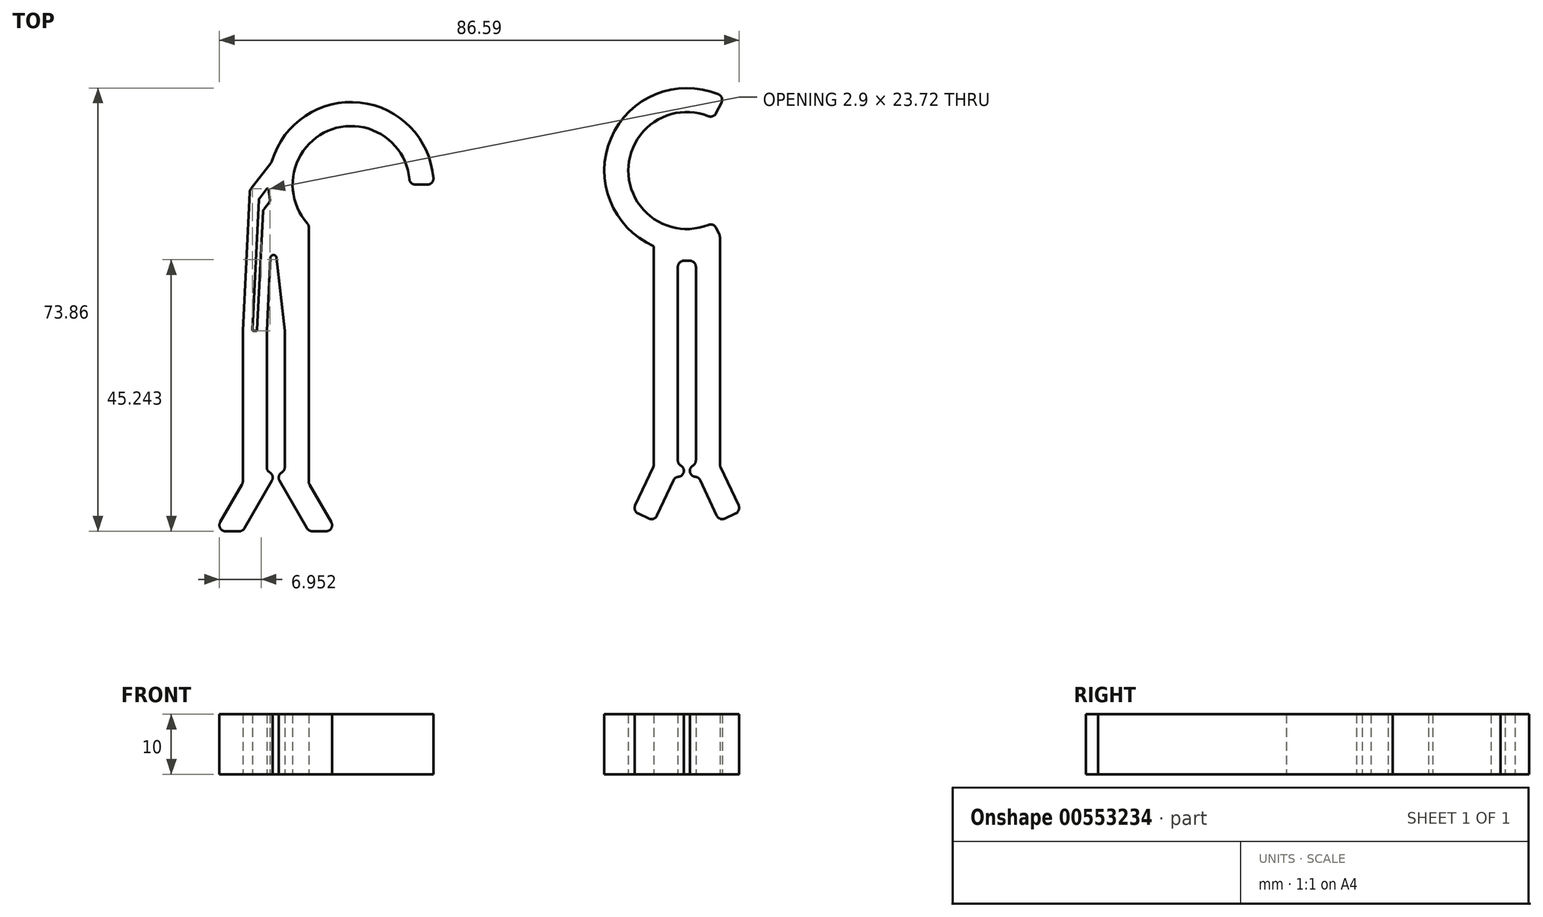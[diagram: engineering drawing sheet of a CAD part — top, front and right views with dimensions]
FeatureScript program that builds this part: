
annotation { "Feature Type Name" : "Feature", "Feature Type Description" : "" }
export const myFeature = defineFeature(function(context is Context, id is Id, definition is map)
    precondition{}
    {
        {
            var Q0;
            Q0=qCreatedBy(makeId("Top.planeOp"),FACE);
            var sketch = newSketch(context, id + "F0", { "sketchPlane" : qUnion([Q0])});
            skArc(sketch, "E0", {"start": v(-22.14, 7.9) * mm, "mid": v(-35.71, 15.97) * mm, "end": v(-39.15, 0.56) * mm});
            skArc(sketch, "E1", {"start": v(-18.14, 8.07) * mm, "mid": v(-30.38, 20.69) * mm, "end": v(-45.02, 10.95) * mm});
            skLineSegment(sketch, "E2", {"start": v(-42.9, -17.37) * mm, "end": v(-42.9, -40.1) * mm});
            skLineSegment(sketch, "E3", {"start": v(-38.9, -4.79) * mm, "end": v(-38.9, -0.1) * mm});
            skLineSegment(sketch, "E4", {"start": v(-21.16, 7.02) * mm, "end": v(-19.12, 7.02) * mm});
            skLineSegment(sketch, "E5", {"start": v(-49.9, -41.7) * mm, "end": v(-49.9, -17.37) * mm});
            skLineSegment(sketch, "E6", {"start": v(-42.9, -17.37) * mm, "end": v(-44.3, -5.15) * mm});
            skPoint(sketch, "E7.visualSharp", {"position": v(-18.1, 7.02) * mm});
            skArc(sketch, "E7.filletArc", {"start": v(-19.12, 7.02) * mm, "mid": v(-18.4, 7.33) * mm, "end": v(-18.14, 8.07) * mm});
            skPoint(sketch, "E8.visualSharp", {"position": v(-22.1, 7.02) * mm});
            skArc(sketch, "E8.filletArc", {"start": v(-22.14, 7.9) * mm, "mid": v(-21.82, 7.27) * mm, "end": v(-21.16, 7.02) * mm});
            skPoint(sketch, "E9.visualSharp", {"position": v(-38.9, 0.29) * mm});
            skArc(sketch, "E9.filletArc", {"start": v(-38.9, -0.1) * mm, "mid": v(-38.97, 0.25) * mm, "end": v(-39.15, 0.56) * mm});
            skArc(sketch, "E10", {"start": v(-45.04, -42.33) * mm, "mid": v(-44.94, -41.57) * mm, "end": v(-45.4, -40.96) * mm});
            skArc(sketch, "E11", {"start": v(-43.4, -40.96) * mm, "mid": v(-43.87, -41.57) * mm, "end": v(-43.77, -42.33) * mm});
            skLineSegment(sketch, "E12.trimOffspring", {"start": v(-45.9, -40.1) * mm, "end": v(-45.9, -17.37) * mm});
            skPoint(sketch, "E13.visualSharp", {"position": v(-42.9, -40.83) * mm});
            skArc(sketch, "E13.filletArc", {"start": v(-43.4, -40.96) * mm, "mid": v(-43.04, -40.6) * mm, "end": v(-42.9, -40.1) * mm});
            skPoint(sketch, "E14.visualSharp", {"position": v(-45.9, -40.83) * mm});
            skArc(sketch, "E14.filletArc", {"start": v(-45.9, -40.1) * mm, "mid": v(-45.77, -40.6) * mm, "end": v(-45.4, -40.96) * mm});
            skLineSegment(sketch, "E15", {"start": v(-45.9, -17.37) * mm, "end": v(-45.3, -5.18) * mm});
            skLineSegment(sketch, "E16", {"start": v(-47.5, -17.18) * mm, "end": v(-46.7, -1.36) * mm});
            skLineSegment(sketch, "E17", {"start": v(-49.9, -17.37) * mm, "end": v(-48.97, 1.3) * mm});
            skLineSegment(sketch, "E18", {"start": v(-48.28, -17) * mm, "end": v(-47.47, -0.76) * mm});
            skLineSegment(sketch, "E19", {"start": v(-48.28, -17) * mm, "end": v(-48.3, -17.16) * mm});
            skLineSegment(sketch, "E20", {"start": v(-48.1, -17.37) * mm, "end": v(-47.7, -17.37) * mm});
            skLineSegment(sketch, "E21", {"start": v(-46.7, -1.36) * mm, "end": v(-46.5, 2.6) * mm});
            skLineSegment(sketch, "E22", {"start": v(-46.4, 2.88) * mm, "end": v(-45.5, 4.05) * mm});
            skLineSegment(sketch, "E23", {"start": v(-47.47, -0.76) * mm, "end": v(-47.2, 4.48) * mm});
            skLineSegment(sketch, "E24", {"start": v(-47.1, 4.76) * mm, "end": v(-45.93, 6.28) * mm});
            skLineSegment(sketch, "E25", {"start": v(-48.97, 1.3) * mm, "end": v(-48.75, 5.75) * mm});
            skLineSegment(sketch, "E26", {"start": v(-48.54, 6.31) * mm, "end": v(-45.2, 10.62) * mm});
            skArc(sketch, "E27.trimOffspring", {"start": v(-45.57, 6.17) * mm, "mid": v(-45.54, 5.81) * mm, "end": v(-45.5, 5.46) * mm});
            skLineSegment(sketch, "E28.trimOffspring", {"start": v(-45.39, 4.41) * mm, "end": v(-45.5, 5.46) * mm});
            skPoint(sketch, "E29.visualSharp", {"position": v(-45.07, 10.77) * mm});
            skArc(sketch, "E29.filletArc", {"start": v(-45.2, 10.62) * mm, "mid": v(-45.1, 10.78) * mm, "end": v(-45.02, 10.95) * mm});
            skPoint(sketch, "E30.visualSharp", {"position": v(-48.73, 6.07) * mm});
            skArc(sketch, "E30.filletArc", {"start": v(-48.54, 6.31) * mm, "mid": v(-48.69, 6.05) * mm, "end": v(-48.75, 5.75) * mm});
            skPoint(sketch, "E31.visualSharp", {"position": v(-49.9, -42.83) * mm});
            skPoint(sketch, "E32.visualSharp", {"position": v(-44.99, 0.9) * mm});
            skArc(sketch, "E32.filletArc", {"start": v(-44.3, -5.15) * mm, "mid": v(-44.8, -4.7) * mm, "end": v(-45.3, -5.18) * mm});
            skPoint(sketch, "E33.visualSharp", {"position": v(-47.2, 4.64) * mm});
            skArc(sketch, "E33.filletArc", {"start": v(-47.1, 4.76) * mm, "mid": v(-47.18, 4.63) * mm, "end": v(-47.2, 4.48) * mm});
            skPoint(sketch, "E34.visualSharp", {"position": v(-45.37, 4.21) * mm});
            skArc(sketch, "E34.filletArc", {"start": v(-45.5, 4.05) * mm, "mid": v(-45.4, 4.22) * mm, "end": v(-45.39, 4.41) * mm});
            skPoint(sketch, "E35.visualSharp", {"position": v(-46.5, 2.75) * mm});
            skArc(sketch, "E35.filletArc", {"start": v(-46.4, 2.88) * mm, "mid": v(-46.48, 2.75) * mm, "end": v(-46.5, 2.6) * mm});
            skPoint(sketch, "E36.visualSharp", {"position": v(-48.3, -17.37) * mm});
            skArc(sketch, "E36.filletArc", {"start": v(-48.3, -17.16) * mm, "mid": v(-48.24, -17.3) * mm, "end": v(-48.1, -17.37) * mm});
            skPoint(sketch, "E37.visualSharp", {"position": v(-47.5, -17.37) * mm});
            skArc(sketch, "E37.filletArc", {"start": v(-47.7, -17.37) * mm, "mid": v(-47.56, -17.31) * mm, "end": v(-47.5, -17.18) * mm});
            skPoint(sketch, "E38.visualSharp", {"position": v(-45.6, 6.7) * mm});
            skArc(sketch, "E38.filletArc", {"start": v(-45.57, 6.17) * mm, "mid": v(-45.71, 6.35) * mm, "end": v(-45.93, 6.28) * mm});
            skLineSegment(sketch, "E39", {"start": v(-49.9, -41.7) * mm, "end": v(-49.9, -42.49) * mm});
            skLineSegment(sketch, "E40", {"start": v(-49.61, -50.25) * mm, "end": v(-45.04, -42.33) * mm});
            skLineSegment(sketch, "E41", {"start": v(-43.77, -42.33) * mm, "end": v(-39.2, -50.25) * mm});
            skPoint(sketch, "E42.start.orphan", {"position": v(-45.9, -42.83) * mm});
            skPoint(sketch, "E43.orphan", {"position": v(-42.9, -42.83) * mm});
            skLineSegment(sketch, "E44", {"start": v(-53.66, -49.25) * mm, "end": v(-50.04, -42.99) * mm});
            skLineSegment(sketch, "E45", {"start": v(-50.48, -50.75) * mm, "end": v(-52.79, -50.75) * mm});
            skPoint(sketch, "E46.visualSharp", {"position": v(-49.9, -50.75) * mm});
            skArc(sketch, "E46.filletArc", {"start": v(-50.48, -50.75) * mm, "mid": v(-49.98, -50.62) * mm, "end": v(-49.61, -50.25) * mm});
            skPoint(sketch, "E47.visualSharp", {"position": v(-54.52, -50.75) * mm});
            skArc(sketch, "E47.filletArc", {"start": v(-53.66, -49.25) * mm, "mid": v(-53.66, -50.25) * mm, "end": v(-52.79, -50.75) * mm});
            skPoint(sketch, "E48.visualSharp", {"position": v(-49.9, -42.75) * mm});
            skArc(sketch, "E48.filletArc", {"start": v(-50.04, -42.99) * mm, "mid": v(-49.94, -42.75) * mm, "end": v(-49.9, -42.49) * mm});
            skLineSegment(sketch, "E49", {"start": v(-35.15, -49.25) * mm, "end": v(-38.77, -42.99) * mm});
            skLineSegment(sketch, "E50", {"start": v(-38.33, -50.75) * mm, "end": v(-36.02, -50.75) * mm});
            skPoint(sketch, "E51.visualSharp", {"position": v(-38.9, -50.75) * mm});
            skArc(sketch, "E51.filletArc", {"start": v(-39.2, -50.25) * mm, "mid": v(-38.83, -50.62) * mm, "end": v(-38.33, -50.75) * mm});
            skLineSegment(sketch, "E52", {"start": v(-38.9, -4.79) * mm, "end": v(-38.9, -42.49) * mm});
            skPoint(sketch, "E53.visualSharp", {"position": v(-34.28, -50.75) * mm});
            skArc(sketch, "E53.filletArc", {"start": v(-36.02, -50.75) * mm, "mid": v(-35.15, -50.25) * mm, "end": v(-35.15, -49.25) * mm});
            skPoint(sketch, "E54.visualSharp", {"position": v(-38.9, -42.75) * mm});
            skArc(sketch, "E54.filletArc", {"start": v(-38.9, -42.49) * mm, "mid": v(-38.87, -42.75) * mm, "end": v(-38.77, -42.99) * mm});
            skLineSegment(sketch, "E55", {"start": v(24.1, -5.69) * mm, "end": v(23.6, -5.69) * mm});
            skLineSegment(sketch, "E56", {"start": v(22.6, -6.69) * mm, "end": v(22.6, -38.96) * mm});
            skLineSegment(sketch, "E57", {"start": v(21.87, -42.26) * mm, "end": v(19.11, -48.16) * mm});
            skLineSegment(sketch, "E58", {"start": v(17.78, -48.65) * mm, "end": v(15.97, -47.8) * mm});
            skLineSegment(sketch, "E59", {"start": v(15.49, -46.47) * mm, "end": v(18.5, -40) * mm});
            skLineSegment(sketch, "E60", {"start": v(18.6, -39.58) * mm, "end": v(18.6, -5.69) * mm});
            skLineSegment(sketch, "E61", {"start": v(24.1, -5.69) * mm, "end": v(24.1, -50.13) * mm, "construction": true});
            skPoint(sketch, "E62.end.orphan", {"position": v(25.6, -5.69) * mm});
            skPoint(sketch, "E62.start.orphan", {"position": v(25.24, -40.69) * mm});
            skArc(sketch, "E63", {"start": v(22.68, -41.69) * mm, "mid": v(23.57, -40.9) * mm, "end": v(23.1, -39.82) * mm});
            skPoint(sketch, "E64.visualSharp", {"position": v(18.7, -49.07) * mm});
            skArc(sketch, "E64.filletArc", {"start": v(17.78, -48.65) * mm, "mid": v(18.55, -48.68) * mm, "end": v(19.11, -48.16) * mm});
            skPoint(sketch, "E65.visualSharp", {"position": v(15.06, -47.38) * mm});
            skArc(sketch, "E65.filletArc", {"start": v(15.49, -46.47) * mm, "mid": v(15.45, -47.24) * mm, "end": v(15.97, -47.8) * mm});
            skPoint(sketch, "E66.visualSharp", {"position": v(18.6, -39.8) * mm});
            skArc(sketch, "E66.filletArc", {"start": v(18.5, -40) * mm, "mid": v(18.57, -39.8) * mm, "end": v(18.6, -39.58) * mm});
            skPoint(sketch, "E67.visualSharp", {"position": v(22.6, -39.69) * mm});
            skArc(sketch, "E67.filletArc", {"start": v(22.6, -38.96) * mm, "mid": v(22.73, -39.46) * mm, "end": v(23.1, -39.82) * mm});
            skPoint(sketch, "E68.visualSharp", {"position": v(22.17, -41.6) * mm});
            skArc(sketch, "E68.filletArc", {"start": v(22.68, -41.69) * mm, "mid": v(22.2, -41.86) * mm, "end": v(21.87, -42.26) * mm});
            skPoint(sketch, "E69.visualSharp", {"position": v(22.6, -5.69) * mm});
            skArc(sketch, "E69.filletArc", {"start": v(23.6, -5.69) * mm, "mid": v(22.9, -5.98) * mm, "end": v(22.6, -6.69) * mm});
            skLineSegment(sketch, "E70.MirrorCS", {"start": v(24.1, -5.69) * mm, "end": v(24.6, -5.69) * mm});
            skArc(sketch, "E71.MirrorCS", {"start": v(25.6, -38.96) * mm, "mid": v(25.46, -39.46) * mm, "end": v(25.1, -39.82) * mm});
            skArc(sketch, "E72.MirrorCS", {"start": v(29.7, -40) * mm, "mid": v(29.62, -39.8) * mm, "end": v(29.6, -39.58) * mm});
            skLineSegment(sketch, "E73.MirrorCS", {"start": v(30.41, -48.65) * mm, "end": v(32.22, -47.8) * mm});
            skArc(sketch, "E74.MirrorCS", {"start": v(25.5, -41.69) * mm, "mid": v(24.62, -40.9) * mm, "end": v(25.1, -39.82) * mm});
            skArc(sketch, "E75.MirrorCS", {"start": v(32.7, -46.47) * mm, "mid": v(32.74, -47.24) * mm, "end": v(32.22, -47.8) * mm});
            skArc(sketch, "E76.MirrorCS", {"start": v(30.41, -48.65) * mm, "mid": v(29.65, -48.68) * mm, "end": v(29.08, -48.16) * mm});
            skArc(sketch, "E77.MirrorCS", {"start": v(24.6, -5.69) * mm, "mid": v(25.3, -5.98) * mm, "end": v(25.6, -6.69) * mm});
            skArc(sketch, "E78.MirrorCS", {"start": v(25.5, -41.69) * mm, "mid": v(26, -41.86) * mm, "end": v(26.33, -42.26) * mm});
            skLineSegment(sketch, "E79.MirrorCS", {"start": v(29.6, -39.58) * mm, "end": v(29.6, -5.69) * mm});
            skPoint(sketch, "E80.MirrorP", {"position": v(33.13, -47.38) * mm});
            skPoint(sketch, "E81.MirrorP", {"position": v(29.5, -49.07) * mm});
            skPoint(sketch, "E82.MirrorP", {"position": v(26.02, -41.6) * mm});
            skPoint(sketch, "E83.MirrorP", {"position": v(29.6, -39.8) * mm});
            skPoint(sketch, "E84.MirrorP", {"position": v(25.6, -39.69) * mm});
            skLineSegment(sketch, "E85.MirrorCS", {"start": v(32.7, -46.47) * mm, "end": v(29.7, -40) * mm});
            skLineSegment(sketch, "E86.MirrorCS", {"start": v(26.33, -42.26) * mm, "end": v(29.08, -48.16) * mm});
            skLineSegment(sketch, "E87.MirrorCS", {"start": v(25.6, -6.69) * mm, "end": v(25.6, -38.96) * mm});
            skArc(sketch, "E88", {"start": v(27.7, 18.42) * mm, "mid": v(14.35, 9.36) * mm, "end": v(27.7, 0.3) * mm});
            skLineSegment(sketch, "E89", {"start": v(18.6, -5.69) * mm, "end": v(18.6, -3.25) * mm});
            skLineSegment(sketch, "E90", {"start": v(29.6, -5.69) * mm, "end": v(29.6, -1.68) * mm});
            skLineSegment(sketch, "E91", {"start": v(28.96, -0.18) * mm, "end": v(29.49, -1.22) * mm});
            skLineSegment(sketch, "E92", {"start": v(24.1, 9.36) * mm, "end": v(44.8, 9.36) * mm, "construction": true});
            skLineSegment(sketch, "E93", {"start": v(28.96, 18.9) * mm, "end": v(29.87, 20.68) * mm});
            skArc(sketch, "E94.trimOffspring", {"start": v(29.36, 22.06) * mm, "mid": v(11.44, 14.74) * mm, "end": v(18.6, -3.25) * mm});
            skPoint(sketch, "E95.visualSharp", {"position": v(29.6, -1.44) * mm});
            skArc(sketch, "E95.filletArc", {"start": v(29.6, -1.68) * mm, "mid": v(29.57, -1.44) * mm, "end": v(29.49, -1.22) * mm});
            skPoint(sketch, "E96.visualSharp", {"position": v(28.52, 0.67) * mm});
            skArc(sketch, "E96.filletArc", {"start": v(28.96, -0.18) * mm, "mid": v(28.42, 0.3) * mm, "end": v(27.7, 0.3) * mm});
            skPoint(sketch, "E97.visualSharp", {"position": v(28.52, 18.04) * mm});
            skArc(sketch, "E97.filletArc", {"start": v(27.7, 18.42) * mm, "mid": v(28.42, 18.41) * mm, "end": v(28.96, 18.9) * mm});
            skPoint(sketch, "E98.visualSharp", {"position": v(30.34, 21.6) * mm});
            skArc(sketch, "E98.filletArc", {"start": v(29.87, 20.68) * mm, "mid": v(29.91, 21.48) * mm, "end": v(29.36, 22.06) * mm});
            skSolve(sketch);
        }
        {
            var Q0;
            Q0 = qSketchRegion(id + "F0", true);
            extrude(context, id + "F1", {"entities" : qUnion([Q0]), "depth" : 10 * mm, "offsetDistance" : 25 * mm});
        }
    });
